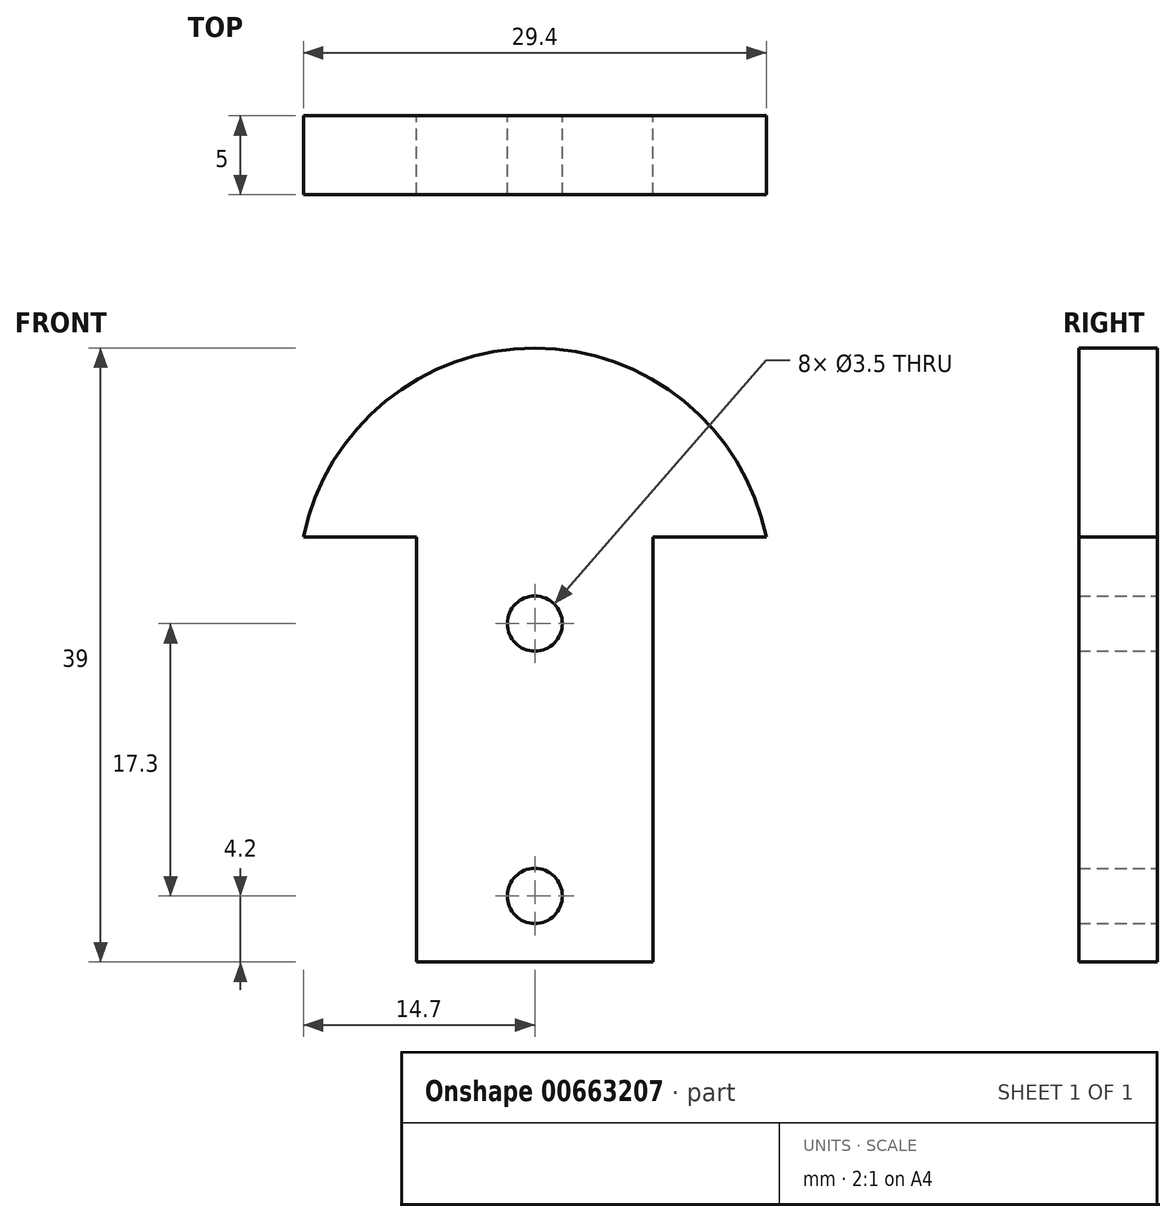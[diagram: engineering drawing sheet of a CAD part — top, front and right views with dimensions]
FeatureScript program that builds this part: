
annotation { "Feature Type Name" : "Feature", "Feature Type Description" : "" }
export const myFeature = defineFeature(function(context is Context, id is Id, definition is map)
    precondition{}
    {
        {
            var Q0;
            Q0=qCreatedBy(makeId("Front.planeOp"),FACE);
            var sketch = newSketch(context, id + "F0", { "sketchPlane" : qUnion([Q0])});
            skLineSegment(sketch, "E0.bottom", {"start": v(7.5, 13.5) * mm, "end": v(-7.5, 13.5) * mm});
            skLineSegment(sketch, "E0.top", {"start": v(7.5, -13.5) * mm, "end": v(-7.5, -13.5) * mm});
            skLineSegment(sketch, "E0.left", {"start": v(7.5, 13.5) * mm, "end": v(7.5, -13.5) * mm});
            skLineSegment(sketch, "E0.right", {"start": v(-7.5, 13.5) * mm, "end": v(-7.5, -13.5) * mm});
            skPoint(sketch, "E0.middle", {"position": v(0, 0) * mm});
            skArc(sketch, "E1", {"start": v(14.7, 13.5) * mm, "mid": v(0, 25.5) * mm, "end": v(-14.7, 13.5) * mm});
            skLineSegment(sketch, "E2", {"start": v(-14.7, 13.5) * mm, "end": v(-7.5, 13.5) * mm});
            skLineSegment(sketch, "E3", {"start": v(7.5, 13.5) * mm, "end": v(14.7, 13.5) * mm});
            skCircle(sketch, "E4", {"center": v(0, 8) * mm, "radius": 1.75 * mm});
            skCircle(sketch, "E5", {"center": v(0, -9.3) * mm, "radius": 1.75 * mm});
            skSolve(sketch);
        }
        {
            var Q0;
            Q0=qSketchRegion(id+"F0",true);
            extrude(context, id + "F1", {"entities" : qUnion([Q0]), "depth" : 5 * mm, "offsetDistance" : 25 * mm});
        }
    });
